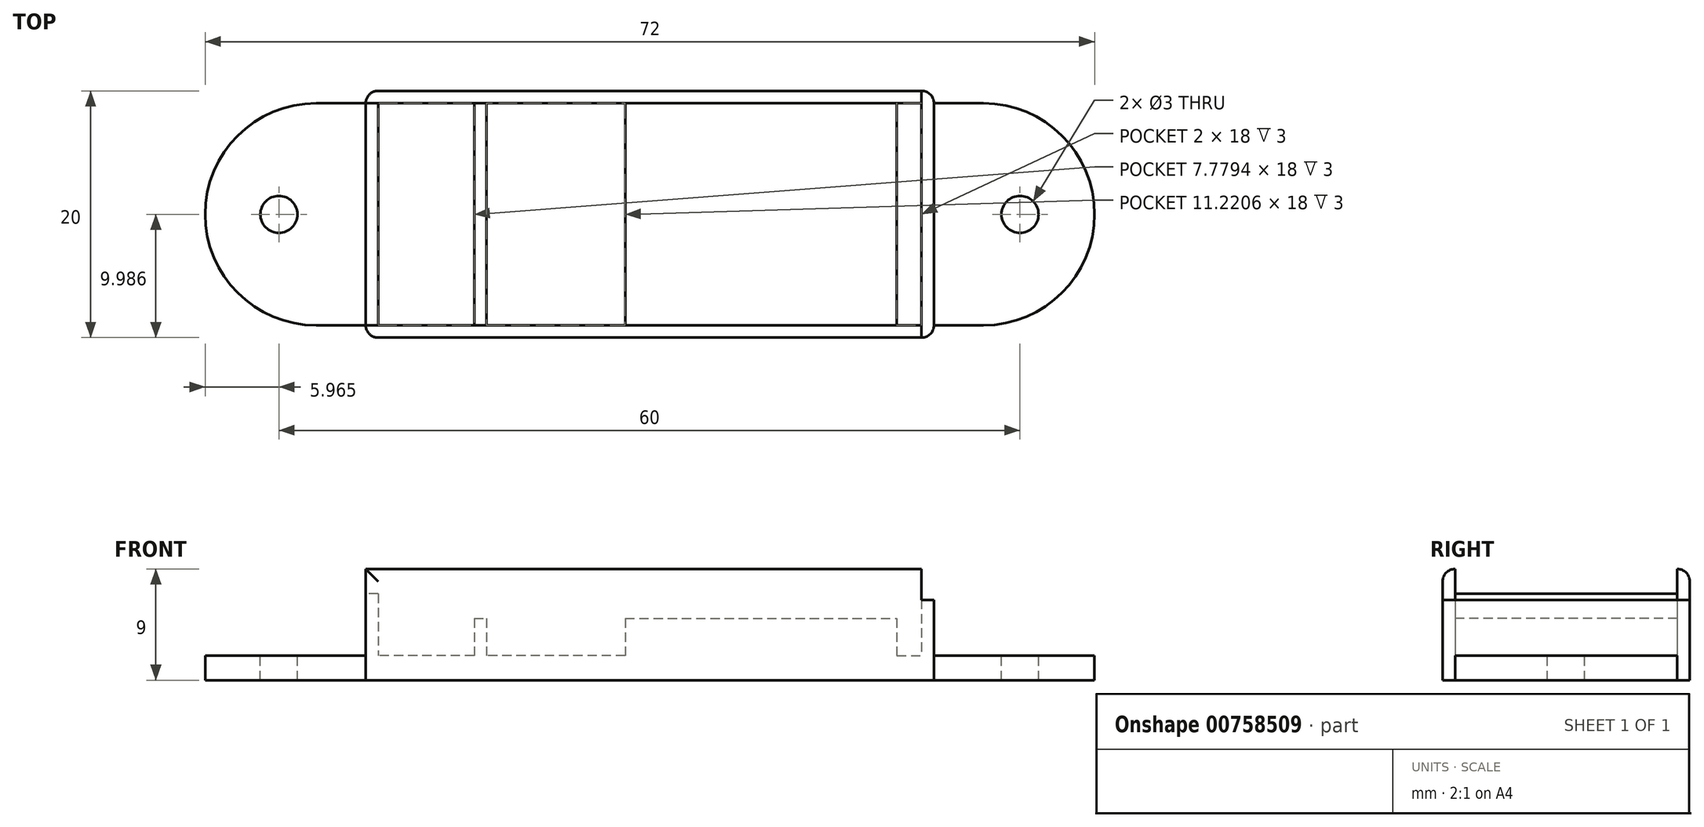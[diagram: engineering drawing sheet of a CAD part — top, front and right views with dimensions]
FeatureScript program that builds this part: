
annotation { "Feature Type Name" : "Feature", "Feature Type Description" : "" }
export const myFeature = defineFeature(function(context is Context, id is Id, definition is map)
    precondition{}
    {
        {
            var Q0;
            Q0=qCreatedBy(makeId("Top.planeOp"),FACE);
            var sketch = newSketch(context, id + "F0", { "sketchPlane" : qUnion([Q0])});
            skLineSegment(sketch, "E0.bottom", {"start": v(-36.22, 7.03) * mm, "end": v(7.78, 7.03) * mm});
            skLineSegment(sketch, "E0.top", {"start": v(-36.22, -10.97) * mm, "end": v(7.78, -10.97) * mm});
            skLineSegment(sketch, "E0.left", {"start": v(-36.22, 7.03) * mm, "end": v(-36.22, -10.97) * mm});
            skLineSegment(sketch, "E0.right", {"start": v(7.78, 7.03) * mm, "end": v(7.78, -10.97) * mm});
            skLineSegment(sketch, "E1.0", {"start": v(-37.22, 8.03) * mm, "end": v(8.78, 8.03) * mm});
            skLineSegment(sketch, "E1.1", {"start": v(-37.22, 8.03) * mm, "end": v(-37.22, -11.97) * mm});
            skLineSegment(sketch, "E1.2", {"start": v(-37.22, -11.97) * mm, "end": v(8.78, -11.97) * mm});
            skLineSegment(sketch, "E1.3", {"start": v(8.78, 8.03) * mm, "end": v(8.78, -11.97) * mm});
            skLineSegment(sketch, "E2", {"start": v(7.78, 7.03) * mm, "end": v(7.78, 8.03) * mm});
            skLineSegment(sketch, "E3", {"start": v(7.78, -10.97) * mm, "end": v(7.78, -11.97) * mm});
            skLineSegment(sketch, "E4", {"start": v(7.78, 2.03) * mm, "end": v(5.78, 2.03) * mm, "construction": true});
            skLineSegment(sketch, "E5", {"start": v(5.78, 7.03) * mm, "end": v(5.78, -10.97) * mm});
            skLineSegment(sketch, "E6.0", {"start": v(4.78, 7.03) * mm, "end": v(4.78, -10.97) * mm});
            skLineSegment(sketch, "E7", {"start": v(-36.22, 4.46) * mm, "end": v(-16.22, 4.46) * mm, "construction": true});
            skLineSegment(sketch, "E8", {"start": v(-36.22, -6.67) * mm, "end": v(-28.22, -6.67) * mm, "construction": true});
            skLineSegment(sketch, "E9", {"start": v(-28.44, 7.03) * mm, "end": v(-28.44, -10.97) * mm});
            skLineSegment(sketch, "E10.0", {"start": v(-27.44, 7.03) * mm, "end": v(-27.44, -10.97) * mm});
            skLineSegment(sketch, "E11", {"start": v(-16.22, 7.03) * mm, "end": v(-16.22, -10.97) * mm});
            skLineSegment(sketch, "E12.0", {"start": v(-15.22, 7.03) * mm, "end": v(-15.22, -10.98) * mm});
            skLineSegment(sketch, "E13", {"start": v(-36.22, 7.03) * mm, "end": v(-37.22, 7.03) * mm});
            skLineSegment(sketch, "E14", {"start": v(-36.22, -10.97) * mm, "end": v(-37.22, -10.97) * mm});
            skLineSegment(sketch, "E15", {"start": v(7.78, 7.03) * mm, "end": v(8.78, 7.03) * mm, "construction": true});
            skLineSegment(sketch, "E16", {"start": v(7.78, -10.97) * mm, "end": v(8.78, -10.97) * mm, "construction": true});
            skPoint(sketch, "E17.startSnap0", {"position": v(-46.44, -1.97) * mm});
            skLineSegment(sketch, "E18", {"start": v(-50.42, 26.35) * mm, "end": v(-50.42, -13.65) * mm, "construction": true});
            skLineSegment(sketch, "E19", {"start": v(-44.26, -1.98) * mm, "end": v(15.74, -1.98) * mm, "construction": true});
            skLineSegment(sketch, "E20.bottom", {"start": v(-37.22, 7.03) * mm, "end": v(-41.22, 7.03) * mm});
            skLineSegment(sketch, "E20.top", {"start": v(-37.22, -10.97) * mm, "end": v(-41.22, -10.97) * mm});
            skLineSegment(sketch, "E20.left", {"start": v(-37.22, 7.03) * mm, "end": v(-37.22, -10.97) * mm});
            skLineSegment(sketch, "E20.right", {"start": v(-41.22, 7.03) * mm, "end": v(-41.22, -10.97) * mm});
            skLineSegment(sketch, "E21.bottom", {"start": v(8.78, 7.03) * mm, "end": v(12.78, 7.03) * mm});
            skLineSegment(sketch, "E21.top", {"start": v(8.78, -10.97) * mm, "end": v(12.78, -10.97) * mm});
            skLineSegment(sketch, "E21.left", {"start": v(8.78, 7.03) * mm, "end": v(8.78, -10.97) * mm});
            skLineSegment(sketch, "E21.right", {"start": v(12.78, 7.03) * mm, "end": v(12.78, -10.97) * mm});
            skArc(sketch, "E22", {"start": v(-41.22, 7.03) * mm, "mid": v(-50.22, -1.97) * mm, "end": v(-41.22, -10.97) * mm});
            skArc(sketch, "E23", {"start": v(12.78, -10.97) * mm, "mid": v(21.78, -1.97) * mm, "end": v(12.78, 7.03) * mm});
            skSolve(sketch);
        }
        {
            var Q0;
            {var subQ8=sQuery(id+"F0.wireOp",EDGE,"E0.left");Q0=makeQuery(id+"F0.imprint","IMPRINT",FACE,{"disambiguationData":[TD([[makeQuery(id+"F0.imprint","IMPRINT",EDGE,{"derivedFrom":subQ8}),-1.0]])]});}
            var Q1;
            {var subQ0=sQuery(id+"F0.wireOp",EDGE,"E0.left");Q1=makeQuery(id+"F0.imprint","IMPRINT",FACE,{"disambiguationData":[TD([[makeQuery(id+"F0.imprint","IMPRINT",EDGE,{"derivedFrom":subQ0}),1.0]])]});}
            var Q2;
            {var subQ0=sQuery(id+"F0.wireOp",EDGE,"E9");Q2=makeQuery(id+"F0.imprint","IMPRINT",FACE,{"disambiguationData":[TD([[makeQuery(id+"F0.imprint","IMPRINT",EDGE,{"derivedFrom":subQ0}),1.0]])]});}
            var Q3;
            {var subQ0=sQuery(id+"F0.wireOp",EDGE,"E10.0");Q3=makeQuery(id+"F0.imprint","IMPRINT",FACE,{"disambiguationData":[TD([[makeQuery(id+"F0.imprint","IMPRINT",EDGE,{"derivedFrom":subQ0}),1.0]])]});}
            var Q4;
            {var subQ0=sQuery(id+"F0.wireOp",EDGE,"E6.0");Q4=makeQuery(id+"F0.imprint","IMPRINT",FACE,{"disambiguationData":[TD([[makeQuery(id+"F0.imprint","IMPRINT",EDGE,{"derivedFrom":subQ0}),-1.0]])]});}
            var Q5;
            {var subQ0=sQuery(id+"F0.wireOp",EDGE,"E5");Q5=makeQuery(id+"F0.imprint","IMPRINT",FACE,{"disambiguationData":[TD([[makeQuery(id+"F0.imprint","IMPRINT",EDGE,{"derivedFrom":subQ0}),-1.0]])]});}
            var Q6;
            {var subQ0=sQuery(id+"F0.wireOp",EDGE,"E0.right");Q6=makeQuery(id+"F0.imprint","IMPRINT",FACE,{"disambiguationData":[TD([[makeQuery(id+"F0.imprint","IMPRINT",EDGE,{"derivedFrom":subQ0}),-1.0]])]});}
            var Q7;
            Q7=makeQuery(id+"F0.imprint","IMPRINT",FACE,{"disambiguationData":[TD([[makeQuery(id+"F0.imprint","IMPRINT",EDGE,{"derivedFrom":sQuery(id+"F0.wireOp",EDGE,"E0.right")}),1.0]])]});
            extrude(context, id + "F1", {"entities" : qUnion([Q0, Q1, Q2, Q3, Q4, Q5, Q6, Q7]), "depth" : -2 * mm, "offsetDistance" : 25 * mm});
        }
        {
            var Q0;
            {var subQ0=sQuery(id+"F0.wireOp",EDGE,"E11");Q0=makeQuery(id+"F0.imprint","IMPRINT",FACE,{"disambiguationData":[TD([[makeQuery(id+"F0.imprint","IMPRINT",EDGE,{"derivedFrom":subQ0}),1.0]])]});}
            var Q1;
            {var subQ0=sQuery(id+"F0.wireOp",EDGE,"E9");Q1=makeQuery(id+"F0.imprint","IMPRINT",FACE,{"disambiguationData":[TD([[makeQuery(id+"F0.imprint","IMPRINT",EDGE,{"derivedFrom":subQ0}),1.0]])]});}
            var Q2;
            {var subQ0=sQuery(id+"F0.wireOp",EDGE,"E5");Q2=makeQuery(id+"F0.imprint","IMPRINT",FACE,{"disambiguationData":[TD([[makeQuery(id+"F0.imprint","IMPRINT",EDGE,{"derivedFrom":subQ0}),-1.0]])]});}
            extrude(context, id + "F2", {"entities" : qUnion([Q0, Q1, Q2]), "depth" : 3 * mm, "offsetDistance" : 25 * mm, "hasSecondDirection" : true, "secondDirectionOppositeDirection" : true, "secondDirectionDepth" : 2 * mm});
        }
        {
            var Q0;
            {var subQ4=sQuery(id+"F0.wireOp",EDGE,"E2");Q0=makeQuery(id+"F0.imprint","IMPRINT",FACE,{"disambiguationData":[TD([[makeQuery(id+"F0.imprint","IMPRINT",EDGE,{"derivedFrom":subQ4}),1.0]])]});}
            var Q1;
            {var subQ0=sQuery(id+"F0.wireOp",EDGE,"E3");Q1=makeQuery(id+"F0.imprint","IMPRINT",FACE,{"disambiguationData":[TD([[makeQuery(id+"F0.imprint","IMPRINT",EDGE,{"derivedFrom":subQ0}),-1.0]])]});}
            extrude(context, id + "F3", {"entities" : qUnion([Q0, Q1]), "depth" : 7 * mm, "offsetDistance" : 25 * mm, "hasSecondDirection" : true, "secondDirectionOppositeDirection" : true, "secondDirectionDepth" : 2 * mm});
        }
        {
            var Q0;
            Q0=makeQuery(id+"F0.imprint","IMPRINT",FACE,{"disambiguationData":[TD([[makeQuery(id+"F0.imprint","IMPRINT",EDGE,{"derivedFrom":sQuery(id+"F0.wireOp",EDGE,"E0.left")}),-1.0]])]});
            extrude(context, id + "F4", {"entities" : qUnion([Q0]), "depth" : 5 * mm, "offsetDistance" : 25 * mm, "hasSecondDirection" : true, "secondDirectionOppositeDirection" : true, "secondDirectionDepth" : 2 * mm});
        }
        {
            var Q0;
            Q0=makeQuery(id+"F0.imprint","IMPRINT",FACE,{"disambiguationData":[TD([[makeQuery(id+"F0.imprint","IMPRINT",EDGE,{"derivedFrom":sQuery(id+"F0.wireOp",EDGE,"E0.right")}),1.0]])]});
            extrude(context, id + "F5", {"entities" : qUnion([Q0]), "depth" : 4.5 * mm, "offsetDistance" : 25 * mm, "hasSecondDirection" : true, "secondDirectionOppositeDirection" : true, "secondDirectionDepth" : 2 * mm});
        }
        {
            var Q0;
            Q0=makeQuery(id+"F1.opExtrude","SWEPT_BODY",BODY,{"disambiguationData":[OSD([sQuery(id+"F0.wireOp",EDGE,"E0.bottom"),sQuery(id+"F0.wireOp",EDGE,"E0.top"),sQuery(id+"F0.wireOp",EDGE,"E1.1"),sQuery(id+"F0.wireOp",EDGE,"E11"),sQuery(id+"F0.wireOp",EDGE,"E13"),sQuery(id+"F0.wireOp",EDGE,"E14")])]});
            var Q1;
            Q1=makeQuery(id+"F1.opExtrude","SWEPT_BODY",BODY,{"disambiguationData":[OSD([sQuery(id+"F0.wireOp",EDGE,"E0.bottom"),sQuery(id+"F0.wireOp",EDGE,"E0.top"),sQuery(id+"F0.wireOp",EDGE,"E1.0"),sQuery(id+"F0.wireOp",EDGE,"E1.2"),sQuery(id+"F0.wireOp",EDGE,"E1.3"),sQuery(id+"F0.wireOp",EDGE,"E2"),sQuery(id+"F0.wireOp",EDGE,"E3"),sQuery(id+"F0.wireOp",EDGE,"E12.0")])]});
            var Q2;
            Q2=makeQuery(id+"F2.opExtrude","SWEPT_BODY",BODY,{"disambiguationData":[OSD([sQuery(id+"F0.wireOp",EDGE,"E0.bottom"),sQuery(id+"F0.wireOp",EDGE,"E0.top"),sQuery(id+"F0.wireOp",EDGE,"E9"),sQuery(id+"F0.wireOp",EDGE,"E10.0")])]});
            var Q3;
            Q3=makeQuery(id+"F2.opExtrude","SWEPT_BODY",BODY,{"disambiguationData":[OSD([sQuery(id+"F0.wireOp",EDGE,"E0.bottom"),sQuery(id+"F0.wireOp",EDGE,"E0.top"),sQuery(id+"F0.wireOp",EDGE,"E11"),sQuery(id+"F0.wireOp",EDGE,"E12.0")])]});
            var Q4;
            Q4=makeQuery(id+"F2.opExtrude","SWEPT_BODY",BODY,{"disambiguationData":[OSD([sQuery(id+"F0.wireOp",EDGE,"E0.bottom"),sQuery(id+"F0.wireOp",EDGE,"E0.top"),sQuery(id+"F0.wireOp",EDGE,"E5"),sQuery(id+"F0.wireOp",EDGE,"E6.0")])]});
            var Q5;
            Q5=makeQuery(id+"F3.opExtrude","SWEPT_BODY",BODY,{"disambiguationData":[OSD([sQuery(id+"F0.wireOp",EDGE,"E0.bottom"),sQuery(id+"F0.wireOp",EDGE,"E1.0"),sQuery(id+"F0.wireOp",EDGE,"E1.1"),sQuery(id+"F0.wireOp",EDGE,"E2"),sQuery(id+"F0.wireOp",EDGE,"E13")])]});
            var Q6;
            Q6=makeQuery(id+"F3.opExtrude","SWEPT_BODY",BODY,{"disambiguationData":[OSD([sQuery(id+"F0.wireOp",EDGE,"E0.top"),sQuery(id+"F0.wireOp",EDGE,"E1.1"),sQuery(id+"F0.wireOp",EDGE,"E1.2"),sQuery(id+"F0.wireOp",EDGE,"E3"),sQuery(id+"F0.wireOp",EDGE,"E14")])]});
            var Q7;
            Q7=makeQuery(id+"F4.opExtrude","SWEPT_BODY",BODY,{"disambiguationData":[OSD([sQuery(id+"F0.wireOp",EDGE,"E0.left"),sQuery(id+"F0.wireOp",EDGE,"E1.1"),sQuery(id+"F0.wireOp",EDGE,"E13"),sQuery(id+"F0.wireOp",EDGE,"E14")])]});
            var Q8;
            Q8=makeQuery(id+"F5.opExtrude","SWEPT_BODY",BODY,{"disambiguationData":[OSD([sQuery(id+"F0.wireOp",EDGE,"E0.right"),sQuery(id+"F0.wireOp",EDGE,"E1.0"),sQuery(id+"F0.wireOp",EDGE,"E1.2"),sQuery(id+"F0.wireOp",EDGE,"E1.3"),sQuery(id+"F0.wireOp",EDGE,"E2"),sQuery(id+"F0.wireOp",EDGE,"E3")])]});
            booleanBodies(context, id + "F6", {"operationType" : BooleanOperationType.UNION, "tools" : qUnion([Q0, Q1, Q2, Q3, Q4, Q5, Q6, Q7, Q8])});
        }
        {
            var Q0;
            {var subQ0=sQuery(id+"F0.wireOp",EDGE,"E1.3");var subQ1=sQuery(id+"F0.wireOp",EDGE,"E1.2");Q0=makeQuery(id+"F6.opBoolean","MERGE",EDGE,{"derivedFrom":[makeQuery(id+"F1.opExtrude","SWEPT_EDGE",EDGE,{"disambiguationData":[OSD([subQ1,subQ0])]}),makeQuery(id+"F5.opExtrude","SWEPT_EDGE",EDGE,{"disambiguationData":[OSD([subQ1,subQ0])]})]});}
            var Q1;
            {var subQ0=sQuery(id+"F0.wireOp",EDGE,"E1.3");var subQ1=sQuery(id+"F0.wireOp",EDGE,"E1.0");Q1=makeQuery(id+"F6.opBoolean","MERGE",EDGE,{"derivedFrom":[makeQuery(id+"F1.opExtrude","SWEPT_EDGE",EDGE,{"disambiguationData":[OSD([subQ1,subQ0])]}),makeQuery(id+"F5.opExtrude","SWEPT_EDGE",EDGE,{"disambiguationData":[OSD([subQ1,subQ0])]})]});}
            var Q2;
            Q2=makeQuery(id+"F3.opExtrude","CAP_EDGE",EDGE,{"disambiguationData":[OSD([sQuery(id+"F0.wireOp",EDGE,"E1.2")])],"isStart":false});
            var Q3;
            Q3=makeQuery(id+"F3.opExtrude","CAP_EDGE",EDGE,{"disambiguationData":[OSD([sQuery(id+"F0.wireOp",EDGE,"E1.0")])],"isStart":false});
            var Q4;
            Q4=makeQuery(id+"F3.opExtrude","SWEPT_EDGE",EDGE,{"disambiguationData":[OSD([sQuery(id+"F0.wireOp",EDGE,"E1.1"),sQuery(id+"F0.wireOp",EDGE,"E1.2")])]});
            var Q5;
            Q5=makeQuery(id+"F3.opExtrude","SWEPT_EDGE",EDGE,{"disambiguationData":[OSD([sQuery(id+"F0.wireOp",EDGE,"E1.0"),sQuery(id+"F0.wireOp",EDGE,"E1.1")])]});
            fillet(context, id + "F7", {"entities" : qUnion([Q0, Q1, Q2, Q3, Q4, Q5]), "radius" : 1 * mm, "tangentPropagation" : true, "allowEdgeOverflow" : false});
        }
        {
            var Q0;
            Q0=makeQuery(id+"F0.imprint","IMPRINT",FACE,{"disambiguationData":[TD([[makeQuery(id+"F0.imprint","IMPRINT",EDGE,{"derivedFrom":sQuery(id+"F0.wireOp",EDGE,"E20.right")}),-1.0]])]});
            var Q1;
            Q1=makeQuery(id+"F0.imprint","IMPRINT",FACE,{"disambiguationData":[TD([[makeQuery(id+"F0.imprint","IMPRINT",EDGE,{"derivedFrom":sQuery(id+"F0.wireOp",EDGE,"E20.bottom")}),1.0]])]});
            var Q2;
            Q2=makeQuery(id+"F0.imprint","IMPRINT",FACE,{"disambiguationData":[TD([[makeQuery(id+"F0.imprint","IMPRINT",EDGE,{"derivedFrom":sQuery(id+"F0.wireOp",EDGE,"E21.bottom")}),-1.0]])]});
            var Q3;
            Q3=makeQuery(id+"F0.imprint","IMPRINT",FACE,{"disambiguationData":[TD([[makeQuery(id+"F0.imprint","IMPRINT",EDGE,{"derivedFrom":sQuery(id+"F0.wireOp",EDGE,"E21.right")}),1.0]])]});
            extrude(context, id + "F8", {"entities" : qUnion([Q0, Q1, Q2, Q3]), "operationType" : NewBodyOperationType.ADD, "depth" : -2 * mm, "offsetDistance" : 25 * mm});
        }
        {
            var Q0;
            Q0=sQuery(id+"F0.wireOp",VERTEX,"E19.end");
            var Q1;
            Q1=sQuery(id+"F0.wireOp",VERTEX,"E19.start");
            var Q2;
            Q2=makeQuery(id+"F1.opExtrude","SWEPT_BODY",BODY,{"disambiguationData":[OSD([sQuery(id+"F0.wireOp",EDGE,"E0.bottom"),sQuery(id+"F0.wireOp",EDGE,"E0.top"),sQuery(id+"F0.wireOp",EDGE,"E11"),sQuery(id+"F0.wireOp",EDGE,"E13"),sQuery(id+"F0.wireOp",EDGE,"E14"),sQuery(id+"F0.wireOp",EDGE,"E20.left")])]});
            hole(context, id + "F9", {"style" : HoleStyle.SIMPLE, "endStyle" : HoleEndStyle.BLIND, "holeDiameter" : 3 * mm, "majorDiameter" : 5 * mm, "holeDepth" : 2 * mm, "isTappedThrough" : true, "tappedDepth" : 12 * mm, "tapClearance" : 3, "locations" : qUnion([Q0, Q1]), "scope" : qUnion([Q2])});
        }
    });
